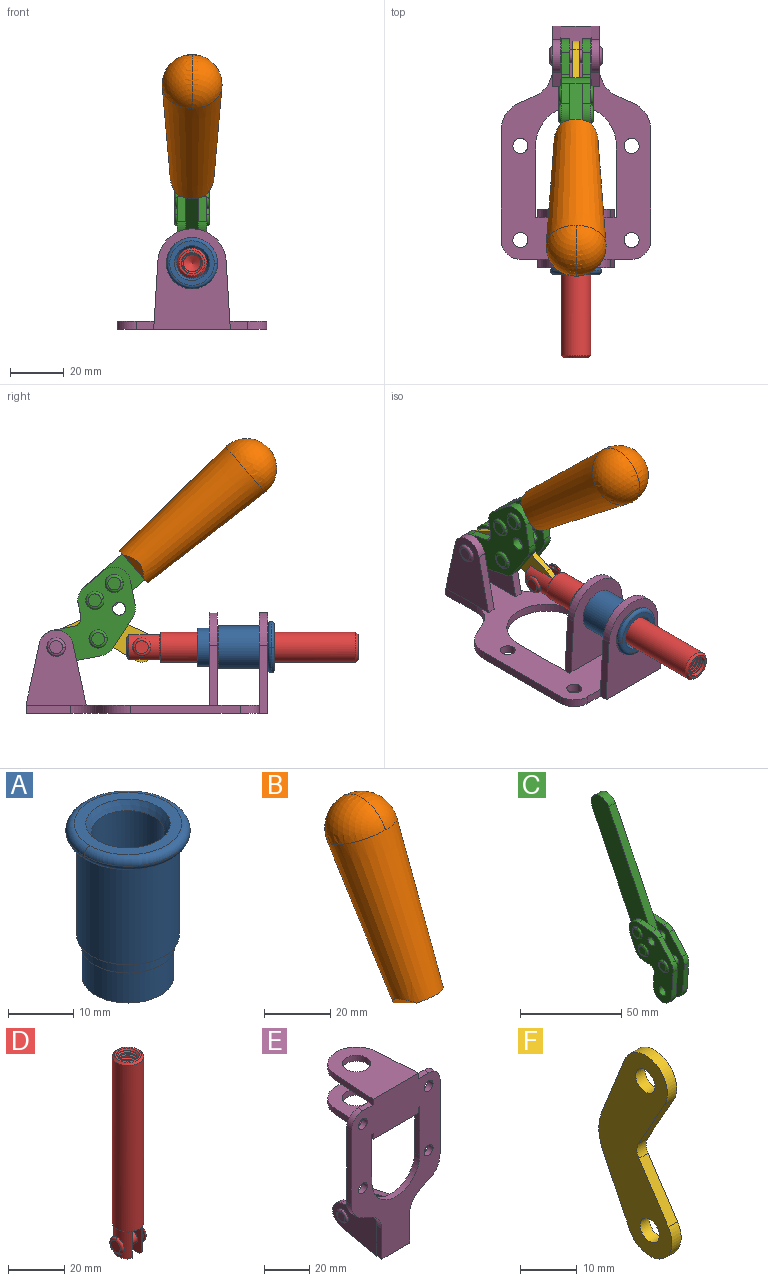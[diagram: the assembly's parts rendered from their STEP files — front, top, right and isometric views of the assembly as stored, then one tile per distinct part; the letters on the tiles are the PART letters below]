
ASSEMBLY  parts=6 mates=6
PART A: 15 faces, bbox 20.6x20.6x28.7 mm
  f0: torus R=8.26mm, axis (0,0,1), area 56.8mm2, adj f1,f10,f12
  f1: torus R=8.26mm, axis (0,0,1), area 56.8mm2, adj f0,f6,f13
  f2: cylinder r=5.59mm len=25.91mm, axis (0,0,1), area 909.6mm2, adj f3,f4
  f3: cone r=6.86mm half-angle=45deg, axis (0,0,-1), area 70.2mm2, adj f2,f14
  f4: cone r=6.47mm half-angle=30deg, axis (0,0,1), area 66.7mm2, adj f2,f13
  f5: cylinder r=7.04mm len=14.07mm, axis (0,0,1), area 252.6mm2, adj f11,f14
  f6: torus R=8.26mm, axis (0,0,1), area 56.8mm2, adj f1,f12,f13
  f7: cylinder r=7.16mm len=14.33mm, axis (0,0,1), area 91.5mm2, adj f9,f11
  f8: cylinder r=7.86mm len=18.42mm, axis (0,0,1), area 909.6mm2, adj f9,f10
  f9: plane 15.72x15.72mm, normal (0,0,-1), area 33mm2, adj f7,f8
  f10: plane 16.51x16.51mm, normal (0,0,-1), area 19.9mm2, adj f0,f8,f12
  f11: plane 14.33x14.33mm, normal (0,0,-1), area 5.7mm2, adj f5,f7
  f12: torus R=8.26mm, axis (0,0,1), area 56.8mm2, adj f0,f6,f10
  f13: plane 16.51x16.51mm, normal (0,0,1), area 82.7mm2, adj f1,f4,f6
  f14: plane 14.07x14.07mm, normal (0,0,-1), area 7.8mm2, adj f3,f5
PART B: 11 faces, bbox 22.3x42.6x64.5 mm
  f0: sphere r=11.13mm, area 411.4mm2, adj f1,f8
  f1: cone r=11.11mm half-angle=3.3deg, axis (0,0.44,0.9), area 3251.8mm2, adj f0,f7,f8,f9,f10
  f2: cylinder r=6.16mm len=11.7mm, axis (1,0,0), area 89.5mm2, adj f3,f4,f5,f6
  f3: plane 60.23x36.75mm, normal (-1,0,0), area 763.6mm2, adj f2,f4,f6,f10
  f4: plane 51.37x25.05mm, normal (0,0.9,-0.44), area 264.2mm2, adj f2,f3,f5,f10
  f5: plane 60.23x36.75mm, normal (1,0,0), area 763.6mm2, adj f2,f4,f6,f10
  f6: plane 51.37x25.05mm, normal (0,-0.9,0.44), area 264.2mm2, adj f2,f3,f5,f10
  f7: plane 9.95x5.95mm, normal (0.71,-0.31,-0.64), area 25.8mm2, adj f1,f10
  f8: sphere r=11.13mm, area 411.4mm2, adj f0,f1
  f9: plane 9.95x5.95mm, normal (-0.71,-0.31,-0.64), area 25.8mm2, adj f1,f10
  f10: plane 14.27x11.38mm, normal (0,-0.44,-0.9), area 106.7mm2, adj f1,f3,f4,f5,f6,f7,f9
PART C: 59 faces, bbox 12.9x60.2x99.6 mm
  f0: torus R=2.39mm, axis (-1,0,0), area 14.9mm2, adj f20,f43,f51
  f1: torus R=2.39mm, axis (-1,0,0), area 14.9mm2, adj f19,f42,f51
  f2: torus R=2.39mm, axis (-1,0,0), area 14.9mm2, adj f18,f35,f51
  f3: torus R=2.39mm, axis (-1,0,0), area 14.9mm2, adj f14,f17,f23
  f4: torus R=2.39mm, axis (-1,0,0), area 14.9mm2, adj f13,f16,f23
  f5: torus R=2.39mm, axis (-1,0,0), area 14.9mm2, adj f12,f15,f23
  f6: cylinder r=2.39mm len=4.78mm, axis (1,0,0), area 46.5mm2, adj f48,f50,f51
  f7: cylinder r=2.39mm len=4.78mm, axis (1,0,0), area 46.5mm2, adj f50,f51
  f8: cylinder r=6.35mm len=12.68mm, axis (1,0,0), area 61.8mm2, adj f38,f39,f50,f51
  f9: cylinder r=2.39mm len=4.78mm, axis (-1,0,0), area 70.5mm2, adj f46,f50
  f10: cylinder r=2.39mm len=4.78mm, axis (-1,0,0), area 46.5mm2, adj f23,f45,f46
  f11: cylinder r=2.39mm len=4.78mm, axis (-1,0,0), area 46.5mm2, adj f23,f46
  f12: plane 4.78x4.78mm, normal (1,0,0), area 17.9mm2, adj f5,f15
  f13: plane 4.78x4.78mm, normal (1,0,0), area 17.9mm2, adj f4,f16
  f14: plane 4.78x4.78mm, normal (1,0,0), area 17.9mm2, adj f3,f17
  f15: torus R=2.39mm, axis (-1,0,0), area 14.9mm2, adj f5,f12,f23
  f16: torus R=2.39mm, axis (-1,0,0), area 14.9mm2, adj f4,f13,f23
  f17: torus R=2.39mm, axis (-1,0,0), area 14.9mm2, adj f3,f14,f23
  f18: plane 4.78x4.78mm, normal (-1,0,0), area 17.9mm2, adj f2,f35
  f19: plane 4.78x4.78mm, normal (-1,0,0), area 17.9mm2, adj f1,f42
  f20: plane 4.78x4.78mm, normal (-1,0,0), area 17.9mm2, adj f0,f43
  f21: plane 2.26x0.2mm, normal (1,0,0), area 0.2mm2, adj f31,f44
  f22: plane 2.26x0.2mm, normal (-1,0,0), area 0.2mm2, adj f41,f44
  f23: plane 39.37x30.77mm, normal (1,0,0), area 565.5mm2, adj f3,f4,f5,f10,f11,f15,f16,f17
  f24: cylinder r=6.1mm len=4.15mm, axis (-1,0,0), area 14.7mm2, adj f23,f25,f32,f46
  f25: plane 10.25x9.01mm, normal (0,-0.75,0.66), area 42.3mm2, adj f23,f24,f26,f46
  f26: cylinder r=6.35mm len=4.64mm, axis (-1,0,0), area 15.6mm2, adj f23,f25,f27,f46
  f27: plane 15.84x3.1mm, normal (0,-1,-0.07), area 49.2mm2, adj f23,f26,f28,f46
  f28: cylinder r=6.35mm len=12.68mm, axis (-1,0,0), area 61.8mm2, adj f23,f27,f29,f46
  f29: plane 8.11x3.1mm, normal (0,1,0.07), area 25.2mm2, adj f23,f28,f30,f46
  f30: cylinder r=3.05mm len=3.25mm, axis (-1,0,0), area 14.8mm2, adj f23,f29,f31,f46
  f31: plane 5.99x3.1mm, normal (0,0.07,-1), area 18.6mm2, adj f21,f23,f30,f44,f46
  f32: plane 9.5x3.1mm, normal (0,-0.07,1), area 29.5mm2, adj f23,f24,f33,f46,f47
  f33: cylinder r=6.1mm len=8.63mm, axis (-1,0,0), area 39.1mm2, adj f23,f32,f34,f47
  f34: plane 8.65x3.96mm, normal (0,0.91,-0.42), area 29.5mm2, adj f23,f33,f44,f47
  f35: torus R=2.39mm, axis (-1,0,0), area 14.9mm2, adj f2,f18,f51
  f36: plane 10.25x9.01mm, normal (0,-0.75,0.66), area 42.3mm2, adj f37,f49,f50,f51
  f37: cylinder r=6.35mm len=4.64mm, axis (1,0,0), area 15.6mm2, adj f36,f38,f50,f51
  f38: plane 15.84x3.1mm, normal (0,-1,-0.07), area 49.2mm2, adj f8,f37,f50,f51
  f39: plane 8.11x3.1mm, normal (0,1,0.07), area 25.2mm2, adj f8,f40,f50,f51
  f40: cylinder r=3.05mm len=3.25mm, axis (1,0,0), area 14.8mm2, adj f39,f41,f50,f51
  f41: plane 5.99x3.1mm, normal (0,0.07,-1), area 18.6mm2, adj f22,f40,f44,f50,f51
  f42: torus R=2.39mm, axis (-1,0,0), area 14.9mm2, adj f1,f19,f51
  f43: torus R=2.39mm, axis (-1,0,0), area 14.9mm2, adj f0,f20,f51
  f44: cylinder r=6.35mm len=12.12mm, axis (-1,0,0), area 128.9mm2, adj f21,f22,f23,f31,f34,f41,f46,f47
  f45: plane 2.65x1.35mm, normal (1,0,0), area 1mm2, adj f10,f55
  f46: plane 39.08x20.42mm, normal (-1,0,0), area 412.5mm2, adj f9,f10,f11,f24,f25,f26,f27,f28
  f47: plane 77.62x39.82mm, normal (1,0,0), area 850mm2, adj f32,f33,f34,f44,f53,f54,f55
  f48: plane 2.65x1.35mm, normal (-1,0,0), area 1mm2, adj f6,f55
  f49: cylinder r=6.1mm len=4.15mm, axis (1,0,0), area 14.7mm2, adj f36,f50,f51,f56
  f50: plane 39.08x20.42mm, normal (1,0,0), area 412.5mm2, adj f6,f7,f8,f9,f36,f37,f38,f39
  f51: plane 39.37x30.77mm, normal (-1,0,0), area 565.5mm2, adj f0,f1,f2,f6,f7,f8,f35,f36
  f52: plane 8.65x3.96mm, normal (0,0.91,-0.42), area 29.5mm2, adj f44,f51,f57,f58
  f53: plane 68.49x33.4mm, normal (0,0.9,-0.44), area 358.1mm2, adj f44,f47,f54,f58
  f54: cylinder r=6.35mm len=12.06mm, axis (1,0,0), area 93.7mm2, adj f47,f53,f55,f58
  f55: plane 68.49x33.4mm, normal (0,-0.9,0.44), area 358.1mm2, adj f44,f45,f46,f47,f48,f50,f54,f58
  f56: plane 9.5x3.1mm, normal (0,-0.07,1), area 29.5mm2, adj f49,f50,f51,f57,f58
  f57: cylinder r=6.1mm len=8.63mm, axis (1,0,0), area 39.1mm2, adj f51,f52,f56,f58
  f58: plane 77.62x39.82mm, normal (-1,0,0), area 850mm2, adj f44,f52,f53,f54,f55,f56,f57
PART D: 48 faces, bbox 12.6x11.1x86.1 mm
  f0: torus R=2.41mm, axis (-1,0,0), area 15mm2, adj f30,f32,f34
  f1: torus R=2.41mm, axis (-1,0,0), area 15mm2, adj f29,f31,f33
  f2: cylinder r=5.54mm len=72.39mm, axis (0,0,1), area 2518.5mm2, adj f3,f4,f42,f43
  f3: cone r=5.54mm half-angle=45deg, axis (0,0,1), area 7.6mm2, adj f2,f5,f41
  f4: cone r=5.54mm half-angle=45deg, axis (0,0,-1), area 34.9mm2, adj f2,f39
  f5: cylinder r=5.08mm len=11.48mm, axis (0,0,1), area 108.3mm2, adj f3,f7,f8,f41
  f6: cylinder r=2.41mm len=4.83mm, axis (-1,0,0), area 71.2mm2, adj f40,f41
  f7: cylinder r=2.41mm len=4.83mm, axis (-1,0,0), area 7.6mm2, adj f5,f34
  f8: cone r=5.08mm half-angle=45deg, axis (0,0,1), area 10.6mm2, adj f5,f37,f41
  f9: cone r=3.98mm half-angle=45deg, axis (0,0,1), area 17.6mm2, adj f27,f39,f45,f46,f47
  f10: cylinder r=2.41mm len=4.83mm, axis (-1,0,0), area 7.6mm2, adj f33,f38
  f11: cylinder r=3.2mm len=6.4mm, axis (0,0,1), area 78.4mm2, adj f12,f28,f44,f45,f47
  f12: cylinder r=3.2mm len=6.4mm, axis (0,0,1), area 10.5mm2, adj f11,f13,f45,f47
  f13: cylinder r=3.2mm len=6.4mm, axis (0,0,1), area 10.5mm2, adj f12,f14,f45,f47
  f14: cylinder r=3.2mm len=6.4mm, axis (0,0,1), area 10.5mm2, adj f13,f15,f45,f47
  f15: cylinder r=3.2mm len=6.4mm, axis (0,0,1), area 10.5mm2, adj f14,f16,f45,f47
  f16: cylinder r=3.2mm len=6.4mm, axis (0,0,1), area 10.5mm2, adj f15,f17,f45,f47
  f17: cylinder r=3.2mm len=6.4mm, axis (0,0,1), area 10.5mm2, adj f16,f18,f45,f47
  f18: cylinder r=3.2mm len=6.4mm, axis (0,0,1), area 10.5mm2, adj f17,f19,f45,f47
  f19: cylinder r=3.2mm len=6.4mm, axis (0,0,1), area 10.5mm2, adj f18,f20,f45,f47
  f20: cylinder r=3.2mm len=6.4mm, axis (0,0,1), area 10.5mm2, adj f19,f21,f45,f47
  f21: cylinder r=3.2mm len=6.4mm, axis (0,0,1), area 10.5mm2, adj f20,f22,f45,f47
  f22: cylinder r=3.2mm len=6.4mm, axis (0,0,1), area 10.5mm2, adj f21,f23,f45,f47
  f23: cylinder r=3.2mm len=6.4mm, axis (0,0,1), area 10.5mm2, adj f22,f24,f45,f47
  f24: cylinder r=3.2mm len=6.4mm, axis (0,0,1), area 10.5mm2, adj f23,f25,f45,f47
  f25: cylinder r=3.2mm len=6.4mm, axis (0,0,1), area 10.5mm2, adj f24,f26,f45,f47
  f26: cylinder r=3.2mm len=6.4mm, axis (0,0,1), area 10.5mm2, adj f25,f27,f45,f47
  f27: cylinder r=3.2mm len=6.4mm, axis (0,0,1), area 7.4mm2, adj f9,f26,f45,f47
  f28: cone r=3.2mm half-angle=60deg, axis (0,0,1), area 37.2mm2, adj f11
  f29: plane 4.83x4.83mm, normal (-1,0,0), area 18.3mm2, adj f1,f31
  f30: plane 4.83x4.83mm, normal (1,0,0), area 18.3mm2, adj f0,f32
  f31: torus R=2.41mm, axis (-1,0,0), area 15mm2, adj f1,f29,f33
  f32: torus R=2.41mm, axis (-1,0,0), area 15mm2, adj f0,f30,f34
  f33: plane 6.83x6.83mm, normal (1,0,0), area 18.3mm2, adj f1,f10,f31
  f34: plane 6.83x6.83mm, normal (-1,0,0), area 18.3mm2, adj f0,f7,f32
  f35: cone r=5.08mm half-angle=45deg, axis (0,0,1), area 10.6mm2, adj f36,f38,f40
  f36: plane 7.25x1.97mm, normal (0,0,-1), area 10mm2, adj f35,f40
  f37: plane 7.25x1.97mm, normal (0,0,-1), area 10mm2, adj f8,f41
  f38: cylinder r=5.08mm len=11.48mm, axis (0,0,1), area 108.3mm2, adj f10,f35,f40,f42
  f39: plane 9.55x9.55mm, normal (0,0,1), area 22mm2, adj f4,f9
  f40: plane 12.76x10.09mm, normal (1,0,0), area 95.7mm2, adj f6,f35,f36,f38,f42,f43
  f41: plane 12.76x10.09mm, normal (-1,0,0), area 95.7mm2, adj f3,f5,f6,f8,f37,f43
  f42: cone r=5.54mm half-angle=45deg, axis (0,0,1), area 7.6mm2, adj f2,f38,f40
  f43: plane 11.07x4.7mm, normal (0,0,-1), area 50.4mm2, adj f2,f40,f41
  f44: plane 0.89x0.62mm, normal (-1,0,0), area 0.3mm2, adj f11,f45,f46,f47
  f45: bspline ~24.8x7.63mm, area 266.6mm2, adj f9,f11,f12,f13,f14,f15,f16,f17
  f46: bspline ~24.87x7.63mm, area 73.6mm2, adj f9,f44,f45,f47
  f47: bspline ~24.98x7.63mm, area 272.5mm2, adj f9,f11,f12,f13,f14,f15,f16,f17
PART E: 55 faces, bbox 55.7x37.4x89.8 mm
  f0: torus R=2.41mm, axis (-1,0,0), area 15mm2, adj f11,f15,f25
  f1: torus R=2.41mm, axis (-1,0,0), area 15mm2, adj f10,f12,f22
  f2: cylinder r=2.78mm len=5.56mm, axis (0,-1,0), area 54.2mm2, adj f30,f54
  f3: cylinder r=14.99mm len=29.97mm, axis (0,-1,0), area 145.9mm2, adj f30,f49,f53,f54
  f4: cylinder r=2.78mm len=5.56mm, axis (0,-1,0), area 54.2mm2, adj f30,f54
  f5: cylinder r=2.78mm len=5.56mm, axis (0,-1,0), area 54.2mm2, adj f30,f54
  f6: cylinder r=2.78mm len=5.56mm, axis (0,-1,0), area 54.2mm2, adj f30,f54
  f7: cylinder r=6.35mm len=12.7mm, axis (0,0,1), area 123.6mm2, adj f27,f51
  f8: cylinder r=6.35mm len=12.7mm, axis (0,0,-1), area 124.7mm2, adj f21,f35
  f9: cylinder r=2.41mm len=11.18mm, axis (-1,0,0), area 169.4mm2, adj f16,f19
  f10: plane 4.83x4.83mm, normal (1,0,0), area 18.3mm2, adj f1,f12
  f11: plane 4.83x4.83mm, normal (-1,0,0), area 18.3mm2, adj f0,f15
  f12: torus R=2.41mm, axis (-1,0,0), area 15mm2, adj f1,f10,f22
  f13: cylinder r=6.35mm len=12.41mm, axis (1,0,0), area 53.4mm2, adj f18,f19,f22,f23
  f14: cylinder r=6.35mm len=12.41mm, axis (-1,0,0), area 53.4mm2, adj f16,f17,f24,f25
  f15: torus R=2.41mm, axis (-1,0,0), area 15mm2, adj f0,f11,f25
  f16: plane 27.86x22.35mm, normal (1,0,0), area 425.4mm2, adj f9,f14,f17,f24,f30
  f17: plane 22.86x4.97mm, normal (0,0.21,0.98), area 72.5mm2, adj f14,f16,f25,f30
  f18: plane 22.86x4.97mm, normal (0,0.21,0.98), area 72.5mm2, adj f13,f19,f22,f30
  f19: plane 27.86x22.35mm, normal (-1,0,0), area 425.4mm2, adj f9,f13,f18,f23,f30
  f20: cylinder r=12.7mm len=25.35mm, axis (0,0,-1), area 119.8mm2, adj f21,f34,f35,f36
  f21: plane 34.21x28.07mm, normal (0,0,-1), area 702.4mm2, adj f8,f20,f30,f34,f36
  f22: plane 27.96x22.45mm, normal (1,0,0), area 407.2mm2, adj f1,f12,f13,f18,f23,f30,f42,f43
  f23: plane 22.86x4.97mm, normal (0,0.21,-0.98), area 72.5mm2, adj f13,f19,f22,f44
  f24: plane 22.86x4.97mm, normal (0,0.21,-0.98), area 72.5mm2, adj f14,f16,f25,f44
  f25: plane 27.86x22.35mm, normal (-1,0,0), area 407.1mm2, adj f0,f14,f15,f17,f24,f30,f45,f46
  f26: plane 3.1x0.95mm, normal (0,0,-1), area 2.7mm2, adj f30,f49,f50,f54
  f27: plane 34.21x28.07mm, normal (0,0,1), area 702.4mm2, adj f7,f28,f30,f50,f52
  f28: cylinder r=12.7mm len=25.35mm, axis (0,0,1), area 118.8mm2, adj f27,f50,f51,f52
  f29: plane 3.1x0.95mm, normal (0,0,-1), area 2.7mm2, adj f30,f52,f53,f54
  f30: plane 86.54x55.63mm, normal (0,1,0), area 2362.9mm2, adj f2,f3,f4,f5,f6,f16,f17,f18
  f31: plane 40.56x3.1mm, normal (-1,0,0), area 125.7mm2, adj f30,f32,f48,f54
  f32: cylinder r=7.11mm len=7.11mm, axis (0,-1,0), area 34.6mm2, adj f30,f31,f33,f54
  f33: plane 6.67x3.1mm, normal (0,0,1), area 20.4mm2, adj f30,f32,f34,f54
  f34: plane 25.39x3.13mm, normal (-1,0.06,0), area 79.5mm2, adj f20,f21,f33,f35,f54
  f35: plane 37.31x28.45mm, normal (0,0,1), area 789.9mm2, adj f8,f20,f34,f36,f54
  f36: plane 25.39x3.13mm, normal (1,0.06,0), area 79.5mm2, adj f20,f21,f35,f37,f54
  f37: plane 6.67x3.1mm, normal (0,0,1), area 20.4mm2, adj f30,f36,f38,f54
  f38: cylinder r=7.11mm len=7.11mm, axis (0,-1,0), area 34.6mm2, adj f30,f37,f39,f54
  f39: plane 40.56x3.1mm, normal (1,0,0), area 125.7mm2, adj f30,f38,f40,f54
  f40: cylinder r=11.18mm len=10.16mm, axis (0,-1,0), area 39.5mm2, adj f30,f39,f41,f54
  f41: plane 6.09x3.1mm, normal (0.42,0,-0.91), area 20.8mm2, adj f30,f40,f42,f54
  f42: cylinder r=11.18mm len=9.41mm, axis (0,-1,0), area 37.2mm2, adj f22,f30,f41,f43,f54
  f43: plane 16.5x3.1mm, normal (1,0,0), area 51.1mm2, adj f22,f42,f44,f54
  f44: plane 17.37x3.1mm, normal (0,0,-1), area 53.8mm2, adj f23,f24,f30,f43,f45,f54
  f45: plane 16.5x3.1mm, normal (-1,0,0), area 51.1mm2, adj f25,f44,f46,f54
  f46: cylinder r=11.18mm len=9.41mm, axis (0,-1,0), area 37.2mm2, adj f25,f30,f45,f47,f54
  f47: plane 6.09x3.1mm, normal (-0.42,0,-0.91), area 20.8mm2, adj f30,f46,f48,f54
  f48: cylinder r=11.18mm len=10.16mm, axis (0,-1,0), area 39.5mm2, adj f30,f31,f47,f54
  f49: plane 26.54x3.1mm, normal (-1,0,0), area 82.3mm2, adj f3,f26,f30,f54
  f50: plane 25.39x3.1mm, normal (1,0.06,0), area 78.8mm2, adj f26,f27,f28,f51,f54
  f51: plane 37.31x28.45mm, normal (0,0,-1), area 789.9mm2, adj f7,f28,f50,f52,f54
  f52: plane 25.39x3.1mm, normal (-1,0.06,0), area 78.8mm2, adj f27,f28,f29,f51,f54
  f53: plane 26.54x3.1mm, normal (1,0,0), area 82.3mm2, adj f3,f29,f30,f54
  f54: plane 89.66x55.63mm, normal (0,-1,0), area 2678.5mm2, adj f2,f3,f4,f5,f6,f26,f29,f31
PART F: 12 faces, bbox 2.3x18.2x42.8 mm
  f0: cylinder r=2.4mm len=4.8mm, axis (1,0,0), area 34.9mm2, adj f4,f11
  f1: cylinder r=10.41mm len=8.47mm, axis (1,0,0), area 20.2mm2, adj f4,f9,f10,f11
  f2: cylinder r=3.05mm len=3.16mm, axis (1,0,0), area 7.7mm2, adj f4,f6,f7,f11
  f3: cylinder r=2.4mm len=4.8mm, axis (1,0,0), area 34.9mm2, adj f4,f11
  f4: plane 42.81x18.23mm, normal (-1,0,0), area 414.1mm2, adj f0,f1,f2,f3,f5,f6,f7,f8
  f5: cylinder r=5.54mm len=10.67mm, axis (1,0,0), area 41.8mm2, adj f4,f6,f10,f11
  f6: plane 11.66x6.53mm, normal (0,-0.87,-0.49), area 30.9mm2, adj f2,f4,f5,f11
  f7: plane 11.17x7.33mm, normal (0,-0.84,0.55), area 30.9mm2, adj f2,f4,f8,f11
  f8: cylinder r=5.54mm len=10.51mm, axis (1,0,0), area 41.8mm2, adj f4,f7,f9,f11
  f9: plane 13.67x6.67mm, normal (0,0.9,-0.44), area 35.1mm2, adj f1,f4,f8,f11
  f10: plane 14.1x5.7mm, normal (0,0.93,0.37), area 35.1mm2, adj f1,f4,f5,f11
  f11: plane 42.81x18.23mm, normal (1,0,0), area 414.1mm2, adj f0,f1,f2,f3,f5,f6,f7,f8
PLACE A rot(axis=(1,0,0),90deg) t=(0,9.43,0)mm
PLACE B rot(axis=(1,0,0),75deg) t=(0.04,4.15,9.14)mm
PLACE C rot(axis=(1,0,0),75deg) t=(0,4.15,9.14)mm
PLACE D rot(axis=(1,0,0),90deg) t=(0,25.25,0)mm
PLACE E rot(axis=(1,0,0),90deg) t=(0,9.43,0)mm fixed
PLACE F rot(axis=(1,0,0),92deg) t=(0,26.1,0.55)mm
MATE slider A.f2 <-> D.f2  axis (0,1,0) through (0,-37.98,24.61)mm
MATE revolute E.f0 <-> C.f7  axis (-1,0,0) through (0,41.52,24.61)mm
MATE fastened E.f7 <-> A.f2  axis (0,-1,0) through (0,-36.96,24.61)mm
MATE revolute E.f0 <-> F.f3  axis (-1,0,0) through (0,41.52,24.61)mm
MATE fastened B.f2 <-> C.f54  axis (-1,0,0) through (2.35,-30.37,91.94)mm
MATE revolute F.f5 <-> D.f6  axis (1,0,0) through (0,9.77,24.61)mm
